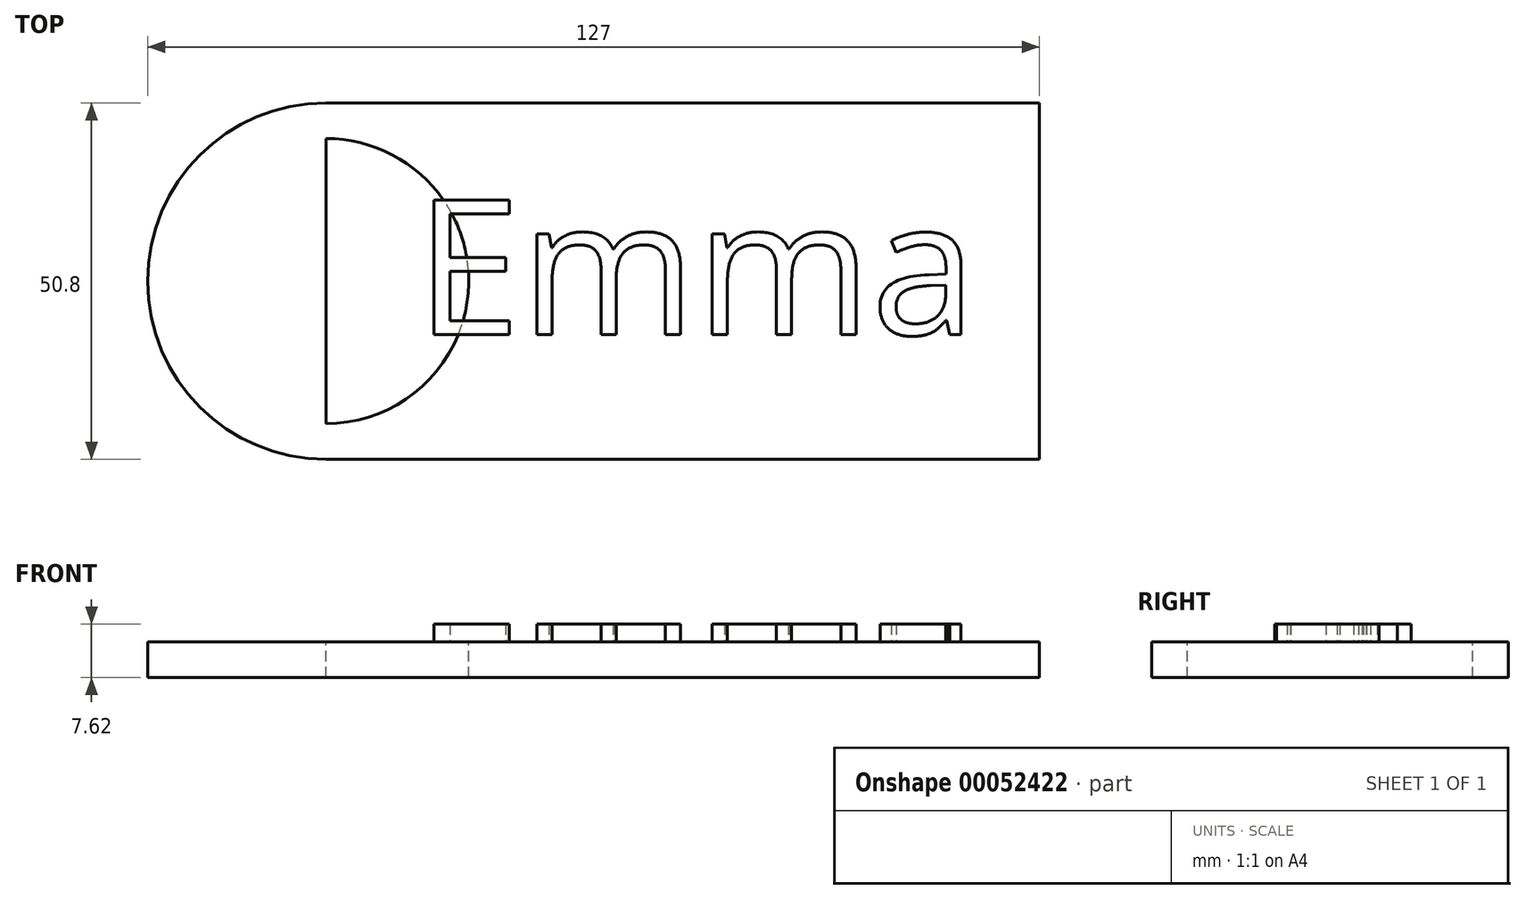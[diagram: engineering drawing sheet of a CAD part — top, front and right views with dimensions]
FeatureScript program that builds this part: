
annotation { "Feature Type Name" : "Feature", "Feature Type Description" : "" }
export const myFeature = defineFeature(function(context is Context, id is Id, definition is map)
    precondition{}
    {
        {
            var Q0;
            Q0=qCreatedBy(makeId("Top.planeOp"),FACE);
            var sketch = newSketch(context, id + "F0", { "sketchPlane" : qUnion([Q0])});
            skLineSegment(sketch, "E0.bottom", {"start": v(-84.9, -27.35) * mm, "end": v(16.7, -27.35) * mm});
            skLineSegment(sketch, "E0.top", {"start": v(-84.9, 23.45) * mm, "end": v(16.7, 23.45) * mm});
            skLineSegment(sketch, "E0.left", {"start": v(-84.9, -27.35) * mm, "end": v(-84.9, 23.45) * mm});
            skLineSegment(sketch, "E0.right", {"start": v(16.7, -27.35) * mm, "end": v(16.7, 23.45) * mm});
            skCircle(sketch, "E1", {"center": v(-84.9, -1.95) * mm, "radius": 25.4 * mm});
            skSolve(sketch);
        }
        {
            var Q0;
            {var subQ0=sQuery(id+"F0.wireOp",EDGE,"E0.left");Q0=makeQuery(id+"F0.imprint","IMPRINT",FACE,{"disambiguationData":[TD([[makeQuery(id+"F0.imprint","IMPRINT",EDGE,{"derivedFrom":subQ0}),1.0]])]});}
            var Q1;
            {var subQ0=sQuery(id+"F0.wireOp",EDGE,"E0.bottom");Q1=makeQuery(id+"F0.imprint","IMPRINT",FACE,{"disambiguationData":[TD([[makeQuery(id+"F0.imprint","IMPRINT",EDGE,{"derivedFrom":subQ0}),1.0]])]});}
            var Q2;
            {var subQ0=sQuery(id+"F0.wireOp",EDGE,"E0.left");Q2=makeQuery(id+"F0.imprint","IMPRINT",FACE,{"disambiguationData":[TD([[makeQuery(id+"F0.imprint","IMPRINT",EDGE,{"derivedFrom":subQ0}),-1.0]])]});}
            extrude(context, id + "F1", {"entities" : qUnion([Q0, Q1, Q2]), "depth" : 5.08 * mm});
        }
        {
            var Q0;
            Q0=makeQuery(id+"F1.opExtrude","CAP_FACE",FACE,{"disambiguationData":[OSD([sQuery(id+"F0.wireOp",EDGE,"E0.bottom"),sQuery(id+"F0.wireOp",EDGE,"E0.top"),sQuery(id+"F0.wireOp",EDGE,"E0.right"),sQuery(id+"F0.wireOp",EDGE,"E1")])],"isStart":false});
            var sketch = newSketch(context, id + "F2", { "sketchPlane" : qUnion([Q0])});
            skCircle(sketch, "E2", {"center": v(-84.9, -1.95) * mm, "radius": 20.32 * mm});
            skLineSegment(sketch, "E3", {"start": v(-84.9, 23.45) * mm, "end": v(-84.9, -27.35) * mm});
            skSolve(sketch);
        }
        {
            var Q0;
            {var subQ0=sQuery(id+"F2.wireOp",EDGE,"E3");var subQ1=sQuery(id+"F2.wireOp",EDGE,"E2");var subQ2=makeQuery(id+"F2.imprint","INTERSECT",VERTEX,{"disambiguationData":[OD(0.0)],"derivedFrom":[subQ1,subQ0]});Q0=makeQuery(id+"F2.imprint","IMPRINT",FACE,{"disambiguationData":[TD([[makeQuery(id+"F2.imprint","IMPRINT",EDGE,{"disambiguationData":[TD([[subQ2,-1.0]])],"derivedFrom":subQ1}),1.0]])]});}
            extrude(context, id + "F3", {"entities" : qUnion([Q0]), "operationType" : NewBodyOperationType.REMOVE, "endBound" : BoundingType.UP_TO_NEXT, "oppositeDirection" : true, "depth" : 25.4 * mm});
        }
        {
            var Q0;
            Q0=makeQuery(id+"F1.opExtrude","CAP_FACE",FACE,{"disambiguationData":[OSD([sQuery(id+"F0.wireOp",EDGE,"E0.bottom"),sQuery(id+"F0.wireOp",EDGE,"E0.top"),sQuery(id+"F0.wireOp",EDGE,"E0.right"),sQuery(id+"F0.wireOp",EDGE,"E1")])],"isStart":false});
            var sketch = newSketch(context, id + "F4", { "sketchPlane" : qUnion([Q0])});
            skText(sketch, "E4", { "text": "Emma", "fontName": "OpenSans-Regular.ttf"});
            const initialGuessF4  = {"E4": [-0.07215, -0.00958, 1, 0, 0.01934]};
            skSetInitialGuess(sketch, initialGuessF4);
            skSolve(sketch);
        }
        {
            var Q0;
            Q0 = qSketchRegion(id + "F4", true);
            extrude(context, id + "F5", {"entities" : qUnion([Q0]), "operationType" : NewBodyOperationType.ADD, "depth" : 2.54 * mm});
        }
    });
